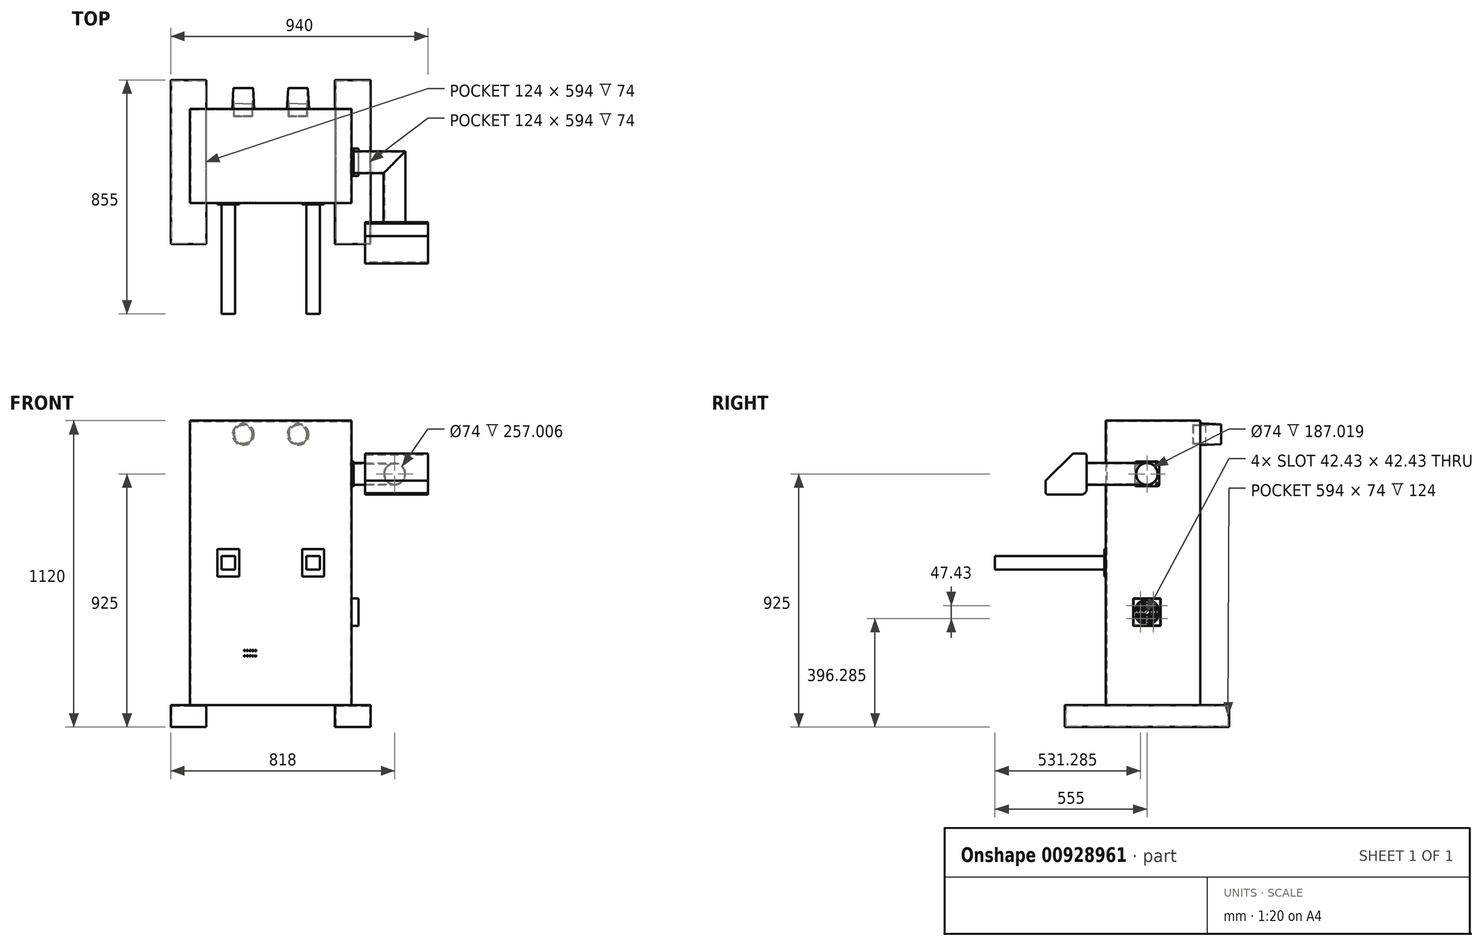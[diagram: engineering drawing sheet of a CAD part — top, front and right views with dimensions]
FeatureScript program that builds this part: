
annotation { "Feature Type Name" : "Feature", "Feature Type Description" : "" }
export const myFeature = defineFeature(function(context is Context, id is Id, definition is map)
    precondition{}
    {
        {
            var Q0;
            Q0=qCreatedBy(makeId("Top.planeOp"),FACE);
            var sketch = newSketch(context, id + "F0", { "sketchPlane" : qUnion([Q0])});
            skLineSegment(sketch, "E0.bottom", {"start": v(-365, 300) * mm, "end": v(-235, 300) * mm});
            skLineSegment(sketch, "E0.top", {"start": v(-365, -300) * mm, "end": v(-235, -300) * mm});
            skLineSegment(sketch, "E0.left", {"start": v(-365, 300) * mm, "end": v(-365, -300) * mm});
            skLineSegment(sketch, "E0.right", {"start": v(-235, 300) * mm, "end": v(-235, -300) * mm});
            skLineSegment(sketch, "E1.bottom", {"start": v(235, 300) * mm, "end": v(365, 300) * mm});
            skLineSegment(sketch, "E1.top", {"start": v(235, -300) * mm, "end": v(365, -300) * mm});
            skLineSegment(sketch, "E1.left", {"start": v(235, 300) * mm, "end": v(235, -300) * mm});
            skLineSegment(sketch, "E1.right", {"start": v(365, 300) * mm, "end": v(365, -300) * mm});
            skLineSegment(sketch, "E2", {"start": v(0, 423) * mm, "end": v(0, -416.4) * mm, "construction": true});
            skLineSegment(sketch, "E3", {"start": v(-423, 0) * mm, "end": v(399.91, 0) * mm, "construction": true});
            skSolve(sketch);
        }
        {
            var Q0;
            Q0 = qSketchRegion(id + "F0", true);
            extrude(context, id + "F1", {"entities" : qUnion([Q0]), "depth" : 80 * mm, "offsetDistance" : 25.4 * mm});
        }
        {
            var Q0;
            Q0=makeQuery(id+"F1.opExtrude","CAP_FACE",FACE,{"disambiguationData":[OSD([sQuery(id+"F0.wireOp",EDGE,"E0.bottom"),sQuery(id+"F0.wireOp",EDGE,"E0.top"),sQuery(id+"F0.wireOp",EDGE,"E0.left"),sQuery(id+"F0.wireOp",EDGE,"E0.right")])],"isStart":false});
            var sketch = newSketch(context, id + "F2", { "sketchPlane" : qUnion([Q0])});
            skLineSegment(sketch, "E4.bottom", {"start": v(-295, 195) * mm, "end": v(295, 195) * mm});
            skLineSegment(sketch, "E4.top", {"start": v(-295, -150) * mm, "end": v(295, -150) * mm});
            skLineSegment(sketch, "E4.left", {"start": v(-295, 195) * mm, "end": v(-295, -150) * mm});
            skLineSegment(sketch, "E4.right", {"start": v(295, 195) * mm, "end": v(295, -150) * mm});
            skSolve(sketch);
        }
        {
            var Q0;
            Q0 = qSketchRegion(id + "F2", true);
            extrude(context, id + "F3", {"entities" : qUnion([Q0]), "operationType" : NewBodyOperationType.ADD, "depth" : 1040 * mm, "offsetDistance" : 25.4 * mm});
        }
        {
            var Q0;
            Q0=makeQuery(id+"F3.opExtrude","SWEPT_FACE",FACE,{"disambiguationData":[OSD([sQuery(id+"F2.wireOp",EDGE,"E4.right")])]});
            var sketch = newSketch(context, id + "F4", { "sketchPlane" : qUnion([Q0])});
            skLineSegment(sketch, "E5.bottom", {"start": v(-38.65, 970) * mm, "end": v(38.65, 970) * mm});
            skLineSegment(sketch, "E5.top", {"start": v(-38.65, 880) * mm, "end": v(38.65, 880) * mm});
            skLineSegment(sketch, "E5.left", {"start": v(-45, 963.65) * mm, "end": v(-45, 886.35) * mm});
            skLineSegment(sketch, "E5.right", {"start": v(45, 963.65) * mm, "end": v(45, 886.35) * mm});
            skLineSegment(sketch, "E6", {"start": v(0, 208.56) * mm, "end": v(0, 602.78) * mm, "construction": true});
            skPoint(sketch, "E7.visualSharp", {"position": v(-45, 970) * mm});
            skArc(sketch, "E7.filletArc", {"start": v(-38.65, 970) * mm, "mid": v(-43.14, 968.14) * mm, "end": v(-45, 963.65) * mm});
            skPoint(sketch, "E8.visualSharp", {"position": v(45, 970) * mm});
            skArc(sketch, "E8.filletArc", {"start": v(45, 963.65) * mm, "mid": v(43.14, 968.14) * mm, "end": v(38.65, 970) * mm});
            skPoint(sketch, "E9.visualSharp", {"position": v(45, 880) * mm});
            skArc(sketch, "E9.filletArc", {"start": v(38.65, 880) * mm, "mid": v(43.14, 881.86) * mm, "end": v(45, 886.35) * mm});
            skPoint(sketch, "E10.visualSharp", {"position": v(-45, 880) * mm});
            skArc(sketch, "E10.filletArc", {"start": v(-45, 886.35) * mm, "mid": v(-43.14, 881.86) * mm, "end": v(-38.65, 880) * mm});
            skSolve(sketch);
        }
        {
            var Q0;
            Q0 = qSketchRegion(id + "F4", true);
            extrude(context, id + "F5", {"entities" : qUnion([Q0]), "operationType" : NewBodyOperationType.ADD, "depth" : 8 * mm, "offsetDistance" : 25.4 * mm});
        }
        {
            var Q0;
            Q0=makeQuery(id+"F5.opExtrude","CAP_FACE",FACE,{"disambiguationData":[OSD([sQuery(id+"F4.wireOp",EDGE,"E5.bottom"),sQuery(id+"F4.wireOp",EDGE,"E5.top"),sQuery(id+"F4.wireOp",EDGE,"E5.left"),sQuery(id+"F4.wireOp",EDGE,"E5.right"),sQuery(id+"F4.wireOp",EDGE,"E7.filletArc"),sQuery(id+"F4.wireOp",EDGE,"E8.filletArc"),sQuery(id+"F4.wireOp",EDGE,"E9.filletArc"),sQuery(id+"F4.wireOp",EDGE,"E10.filletArc")])],"isStart":false});
            var sketch = newSketch(context, id + "F6", { "sketchPlane" : qUnion([Q0])});
            skCircle(sketch, "E11", {"center": v(-38.65, 963.65) * mm, "radius": 5 * mm});
            skCircle(sketch, "E12", {"center": v(38.65, 963.65) * mm, "radius": 5 * mm});
            skCircle(sketch, "E13", {"center": v(38.65, 886.35) * mm, "radius": 5 * mm});
            skCircle(sketch, "E14", {"center": v(-38.65, 886.35) * mm, "radius": 5 * mm});
            skSolve(sketch);
        }
        {
            var Q0;
            Q0 = qSketchRegion(id + "F6", true);
            extrude(context, id + "F7", {"entities" : qUnion([Q0]), "operationType" : NewBodyOperationType.REMOVE, "oppositeDirection" : true, "depth" : 8 * mm, "offsetDistance" : 25.4 * mm});
        }
        {
            var Q0;
            Q0=makeQuery(id+"F5.opExtrude","CAP_FACE",FACE,{"disambiguationData":[OSD([sQuery(id+"F4.wireOp",EDGE,"E5.bottom"),sQuery(id+"F4.wireOp",EDGE,"E5.top"),sQuery(id+"F4.wireOp",EDGE,"E5.left"),sQuery(id+"F4.wireOp",EDGE,"E5.right"),sQuery(id+"F4.wireOp",EDGE,"E7.filletArc"),sQuery(id+"F4.wireOp",EDGE,"E8.filletArc"),sQuery(id+"F4.wireOp",EDGE,"E9.filletArc"),sQuery(id+"F4.wireOp",EDGE,"E10.filletArc")])],"isStart":false});
            var sketch = newSketch(context, id + "F8", { "sketchPlane" : qUnion([Q0])});
            skCircle(sketch, "E15", {"center": v(0, 925) * mm, "radius": 40 * mm});
            skPoint(sketch, "E15.centerSnap0", {"position": v(45, 925) * mm});
            skCircle(sketch, "E16", {"center": v(0, 925) * mm, "radius": 37 * mm});
            skSolve(sketch);
        }
        {
            var Q0;
            Q0=sQuery(id+"F8.wireOp",EDGE,"E16");
            cPlane(context, id + "F9", {"entities" : qUnion([Q0]), "cplaneType" : CPlaneType.LINE_ANGLE, "offset" : 25.4 * mm, "angle" : 0 * degree, "width" : 152.4 * mm, "height" : 152.4 * mm});
        }
        {
            var Q0;
            Q0=qCreatedBy(id+"F9.planeOp",FACE);
            var sketch = newSketch(context, id + "F10", { "sketchPlane" : qUnion([Q0])});
            skLineSegment(sketch, "E17", {"start": v(-303, 925) * mm, "end": v(-453, 925) * mm});
            skSolve(sketch);
        }
        {
            var Q0;
            Q0=makeQuery(id+"F8.imprint","IMPRINT",FACE,{"disambiguationData":[TD([[makeQuery(id+"F8.imprint","IMPRINT",EDGE,{"derivedFrom":sQuery(id+"F8.wireOp",EDGE,"E15")}),-1.0]])]});
            var Q1;
            Q1=sQuery(id+"F10.wireOp",VERTEX,"E17.end");
            cPlane(context, id + "F11", {"entities" : qUnion([Q0, Q1]), "cplaneType" : CPlaneType.PLANE_POINT, "offset" : 25.4 * mm, "width" : 152.4 * mm, "height" : 152.4 * mm});
        }
        {
            var Q0;
            Q0=qCreatedBy(id+"F11.planeOp",FACE);
            var sketch = newSketch(context, id + "F12", { "sketchPlane" : qUnion([Q0])});
            skLineSegment(sketch, "E18", {"start": v(0, 925) * mm, "end": v(-220, 925) * mm});
            skSolve(sketch);
        }
        {
            var Q0;
            Q0=makeQuery(id+"F8.imprint","IMPRINT",FACE,{"disambiguationData":[TD([[makeQuery(id+"F8.imprint","IMPRINT",EDGE,{"derivedFrom":sQuery(id+"F8.wireOp",EDGE,"E15")}),1.0]])]});
            var Q1;
            Q1=sQuery(id+"F10.wireOp",EDGE,"E17");
            var Q2;
            Q2=sQuery(id+"F12.wireOp",EDGE,"E18");
            sweep(context, id + "F13", {"operationType" : NewBodyOperationType.ADD, "profiles" : qUnion([Q0]), "path" : qUnion([Q1, Q2])});
        }
        {
            var Q0;
            Q0=makeQuery(id+"F3.opExtrude","SWEPT_FACE",FACE,{"disambiguationData":[OSD([sQuery(id+"F2.wireOp",EDGE,"E4.right")])]});
            var sketch = newSketch(context, id + "F14", { "sketchPlane" : qUnion([Q0])});
            skLineSegment(sketch, "E19.bottom", {"start": v(-50, 470) * mm, "end": v(50, 470) * mm});
            skLineSegment(sketch, "E19.top", {"start": v(-50, 370) * mm, "end": v(50, 370) * mm});
            skLineSegment(sketch, "E19.left", {"start": v(-50, 470) * mm, "end": v(-50, 370) * mm});
            skLineSegment(sketch, "E19.right", {"start": v(50, 470) * mm, "end": v(50, 370) * mm});
            skLineSegment(sketch, "E20", {"start": v(0, 221.64) * mm, "end": v(0, 996.3) * mm, "construction": true});
            skLineSegment(sketch, "E21.bottom", {"start": v(49, 371) * mm, "end": v(-49, 371) * mm});
            skLineSegment(sketch, "E21.top", {"start": v(49, 469) * mm, "end": v(-49, 469) * mm});
            skLineSegment(sketch, "E21.left", {"start": v(49, 371) * mm, "end": v(49, 469) * mm});
            skLineSegment(sketch, "E21.right", {"start": v(-49, 371) * mm, "end": v(-49, 469) * mm});
            skPoint(sketch, "E21.middle", {"position": v(0, 420) * mm});
            skPoint(sketch, "E21.middle.positionSnap0", {"position": v(50, 420) * mm});
            skPoint(sketch, "E21.centerSnap0", {"position": v(50, 420) * mm});
            skSolve(sketch);
        }
        {
            var Q0;
            Q0 = qSketchRegion(id + "F14", true);
            extrude(context, id + "F15", {"entities" : qUnion([Q0]), "operationType" : NewBodyOperationType.ADD, "depth" : 25.4 * mm, "offsetDistance" : 25.4 * mm});
        }
        {
            var Q0;
            Q0=makeQuery(id+"F15.opExtrude","CAP_FACE",FACE,{"disambiguationData":[OSD([sQuery(id+"F14.wireOp",EDGE,"E19.bottom"),sQuery(id+"F14.wireOp",EDGE,"E19.top"),sQuery(id+"F14.wireOp",EDGE,"E19.left"),sQuery(id+"F14.wireOp",EDGE,"E19.right"),sQuery(id+"F14.wireOp",EDGE,"E21.bottom"),sQuery(id+"F14.wireOp",EDGE,"E21.top"),sQuery(id+"F14.wireOp",EDGE,"E21.left"),sQuery(id+"F14.wireOp",EDGE,"E21.right")])],"isStart":false});
            var sketch = newSketch(context, id + "F16", { "sketchPlane" : qUnion([Q0])});
            skLineSegment(sketch, "E22.bottom", {"start": v(-49, 469) * mm, "end": v(49, 469) * mm});
            skLineSegment(sketch, "E22.top", {"start": v(-49, 371) * mm, "end": v(49, 371) * mm});
            skLineSegment(sketch, "E22.left", {"start": v(-49, 469) * mm, "end": v(-49, 371) * mm});
            skLineSegment(sketch, "E22.right", {"start": v(49, 469) * mm, "end": v(49, 371) * mm});
            skSolve(sketch);
        }
        {
            var Q0;
            Q0 = qSketchRegion(id + "F16", true);
            extrude(context, id + "F17", {"entities" : qUnion([Q0]), "depth" : 1 * mm, "offsetDistance" : 25.4 * mm});
        }
        {
            var Q0;
            Q0=makeQuery(id+"F17.opExtrude","CAP_FACE",FACE,{"disambiguationData":[OSD([sQuery(id+"F16.wireOp",EDGE,"E22.bottom"),sQuery(id+"F16.wireOp",EDGE,"E22.top"),sQuery(id+"F16.wireOp",EDGE,"E22.left"),sQuery(id+"F16.wireOp",EDGE,"E22.right")])],"isStart":false});
            var sketch = newSketch(context, id + "F18", { "sketchPlane" : qUnion([Q0])});
            skCircle(sketch, "E23", {"center": v(0, 420) * mm, "radius": 10 * mm});
            skPoint(sketch, "E23.centerSnap0", {"position": v(49, 420) * mm});
            skArc(sketch, "E24", {"start": v(-2.5, 434.8) * mm, "mid": v(-10.6, 430.6) * mm, "end": v(-14.8, 422.5) * mm});
            skArc(sketch, "E25.0", {"start": v(-2.5, 439.84) * mm, "mid": v(-14.14, 434.14) * mm, "end": v(-19.84, 422.5) * mm});
            skArc(sketch, "E26.0", {"start": v(-2.5, 444.87) * mm, "mid": v(-17.68, 437.68) * mm, "end": v(-24.87, 422.5) * mm});
            skArc(sketch, "E27.0", {"start": v(-2.5, 449.9) * mm, "mid": v(-21.21, 441.21) * mm, "end": v(-29.9, 422.5) * mm});
            skArc(sketch, "E28.0", {"start": v(-2.5, 454.91) * mm, "mid": v(-24.75, 444.75) * mm, "end": v(-34.91, 422.5) * mm});
            skArc(sketch, "E29.0", {"start": v(-2.5, 459.92) * mm, "mid": v(-28.28, 448.28) * mm, "end": v(-39.92, 422.5) * mm});
            skArc(sketch, "E30.0", {"start": v(-2.5, 464.93) * mm, "mid": v(-31.82, 451.82) * mm, "end": v(-44.93, 422.5) * mm});
            skCircle(sketch, "E31.0", {"center": v(0, 420) * mm, "radius": 49 * mm});
            skLineSegment(sketch, "E32", {"start": v(0, 469) * mm, "end": v(0, 375) * mm, "construction": true});
            skLineSegment(sketch, "E33.bottom", {"start": v(-2.5, 469) * mm, "end": v(2.5, 469) * mm});
            skLineSegment(sketch, "E33.left", {"start": v(-2.5, 469) * mm, "end": v(-2.5, 429.68) * mm});
            skLineSegment(sketch, "E33.right", {"start": v(2.5, 469) * mm, "end": v(2.5, 429.68) * mm});
            skPoint(sketch, "E34.orphan", {"position": v(2.5, 420) * mm});
            skLineSegment(sketch, "E35", {"start": v(53.82, 420) * mm, "end": v(-49, 420) * mm, "construction": true});
            skLineSegment(sketch, "E36.bottom", {"start": v(9.68, 422.5) * mm, "end": v(49, 422.5) * mm});
            skLineSegment(sketch, "E36.top", {"start": v(9.68, 417.5) * mm, "end": v(49, 417.5) * mm});
            skLineSegment(sketch, "E36.right", {"start": v(49, 422.5) * mm, "end": v(49, 417.5) * mm});
            skArc(sketch, "E37.trimOffspring", {"start": v(44.93, 422.5) * mm, "mid": v(31.82, 451.82) * mm, "end": v(2.5, 464.93) * mm});
            skArc(sketch, "E38.trimOffspring", {"start": v(39.92, 422.5) * mm, "mid": v(28.28, 448.28) * mm, "end": v(2.5, 459.92) * mm});
            skArc(sketch, "E39.trimOffspring", {"start": v(34.91, 422.5) * mm, "mid": v(24.75, 444.75) * mm, "end": v(2.5, 454.91) * mm});
            skArc(sketch, "E40.trimOffspring", {"start": v(29.9, 422.5) * mm, "mid": v(21.21, 441.21) * mm, "end": v(2.5, 449.9) * mm});
            skArc(sketch, "E41.trimOffspring", {"start": v(24.87, 422.5) * mm, "mid": v(17.68, 437.68) * mm, "end": v(2.5, 444.87) * mm});
            skArc(sketch, "E42.trimOffspring", {"start": v(19.84, 422.5) * mm, "mid": v(14.14, 434.14) * mm, "end": v(2.5, 439.84) * mm});
            skArc(sketch, "E43.trimOffspring", {"start": v(14.8, 422.5) * mm, "mid": v(10.6, 430.6) * mm, "end": v(2.5, 434.8) * mm});
            skPoint(sketch, "E44", {"position": v(0, 371) * mm});
            skLineSegment(sketch, "E45.top", {"start": v(-2.5, 371) * mm, "end": v(2.5, 371) * mm});
            skLineSegment(sketch, "E45.left", {"start": v(-2.5, 410.32) * mm, "end": v(-2.5, 371) * mm});
            skLineSegment(sketch, "E45.right", {"start": v(2.5, 410.32) * mm, "end": v(2.5, 371) * mm});
            skArc(sketch, "E46.trimOffspring", {"start": v(2.5, 375.07) * mm, "mid": v(31.82, 388.18) * mm, "end": v(44.93, 417.5) * mm});
            skArc(sketch, "E47.trimOffspring", {"start": v(2.5, 380.08) * mm, "mid": v(28.28, 391.72) * mm, "end": v(39.92, 417.5) * mm});
            skArc(sketch, "E48.trimOffspring", {"start": v(2.5, 385.09) * mm, "mid": v(24.75, 395.25) * mm, "end": v(34.91, 417.5) * mm});
            skArc(sketch, "E49.trimOffspring", {"start": v(2.5, 390.1) * mm, "mid": v(21.21, 398.79) * mm, "end": v(29.9, 417.5) * mm});
            skArc(sketch, "E50.trimOffspring", {"start": v(2.5, 395.13) * mm, "mid": v(17.68, 402.32) * mm, "end": v(24.87, 417.5) * mm});
            skArc(sketch, "E51.trimOffspring", {"start": v(2.5, 400.16) * mm, "mid": v(14.14, 405.86) * mm, "end": v(19.84, 417.5) * mm});
            skArc(sketch, "E52.trimOffspring", {"start": v(2.5, 405.2) * mm, "mid": v(10.6, 409.4) * mm, "end": v(14.8, 417.5) * mm});
            skLineSegment(sketch, "E53.bottom", {"start": v(-9.68, 422.5) * mm, "end": v(-49, 422.5) * mm});
            skLineSegment(sketch, "E53.top", {"start": v(-9.68, 417.5) * mm, "end": v(-49, 417.5) * mm});
            skLineSegment(sketch, "E53.right", {"start": v(-49, 422.5) * mm, "end": v(-49, 417.5) * mm});
            skArc(sketch, "E54.trimOffspring", {"start": v(-44.93, 417.5) * mm, "mid": v(-31.82, 388.18) * mm, "end": v(-2.5, 375.07) * mm});
            skArc(sketch, "E55.trimOffspring", {"start": v(-39.92, 417.5) * mm, "mid": v(-28.28, 391.72) * mm, "end": v(-2.5, 380.08) * mm});
            skArc(sketch, "E56.trimOffspring", {"start": v(-34.91, 417.5) * mm, "mid": v(-24.75, 395.25) * mm, "end": v(-2.5, 385.09) * mm});
            skArc(sketch, "E57.trimOffspring", {"start": v(-29.9, 417.5) * mm, "mid": v(-21.21, 398.79) * mm, "end": v(-2.5, 390.1) * mm});
            skArc(sketch, "E58.trimOffspring", {"start": v(-24.87, 417.5) * mm, "mid": v(-17.68, 402.32) * mm, "end": v(-2.5, 395.13) * mm});
            skArc(sketch, "E59.trimOffspring", {"start": v(-19.84, 417.5) * mm, "mid": v(-14.14, 405.86) * mm, "end": v(-2.5, 400.16) * mm});
            skArc(sketch, "E60.trimOffspring", {"start": v(-14.8, 417.5) * mm, "mid": v(-10.6, 409.4) * mm, "end": v(-2.5, 405.2) * mm});
            skSolve(sketch);
        }
        {
            var Q0;
            {var subQ0=sQuery(id+"F18.wireOp",EDGE,"E37.trimOffspring");Q0=makeQuery(id+"F18.imprint","IMPRINT",FACE,{"disambiguationData":[TD([[makeQuery(id+"F18.imprint","IMPRINT",EDGE,{"derivedFrom":subQ0}),1.0]])]});}
            var Q1;
            {var subQ0=sQuery(id+"F18.wireOp",EDGE,"E39.trimOffspring");Q1=makeQuery(id+"F18.imprint","IMPRINT",FACE,{"disambiguationData":[TD([[makeQuery(id+"F18.imprint","IMPRINT",EDGE,{"derivedFrom":subQ0}),1.0]])]});}
            var Q2;
            {var subQ0=sQuery(id+"F18.wireOp",EDGE,"E41.trimOffspring");Q2=makeQuery(id+"F18.imprint","IMPRINT",FACE,{"disambiguationData":[TD([[makeQuery(id+"F18.imprint","IMPRINT",EDGE,{"derivedFrom":subQ0}),1.0]])]});}
            var Q3;
            {var subQ5=sQuery(id+"F18.wireOp",EDGE,"E43.trimOffspring");Q3=makeQuery(id+"F18.imprint","IMPRINT",FACE,{"disambiguationData":[TD([[makeQuery(id+"F18.imprint","IMPRINT",EDGE,{"derivedFrom":subQ5}),1.0]])]});}
            var Q4;
            {var subQ0=sQuery(id+"F18.wireOp",EDGE,"E46.trimOffspring");Q4=makeQuery(id+"F18.imprint","IMPRINT",FACE,{"disambiguationData":[TD([[makeQuery(id+"F18.imprint","IMPRINT",EDGE,{"derivedFrom":subQ0}),1.0]])]});}
            var Q5;
            {var subQ0=sQuery(id+"F18.wireOp",EDGE,"E48.trimOffspring");Q5=makeQuery(id+"F18.imprint","IMPRINT",FACE,{"disambiguationData":[TD([[makeQuery(id+"F18.imprint","IMPRINT",EDGE,{"derivedFrom":subQ0}),1.0]])]});}
            var Q6;
            {var subQ0=sQuery(id+"F18.wireOp",EDGE,"E50.trimOffspring");Q6=makeQuery(id+"F18.imprint","IMPRINT",FACE,{"disambiguationData":[TD([[makeQuery(id+"F18.imprint","IMPRINT",EDGE,{"derivedFrom":subQ0}),1.0]])]});}
            var Q7;
            {var subQ5=sQuery(id+"F18.wireOp",EDGE,"E52.trimOffspring");Q7=makeQuery(id+"F18.imprint","IMPRINT",FACE,{"disambiguationData":[TD([[makeQuery(id+"F18.imprint","IMPRINT",EDGE,{"derivedFrom":subQ5}),1.0]])]});}
            var Q8;
            {var subQ0=sQuery(id+"F18.wireOp",EDGE,"E54.trimOffspring");Q8=makeQuery(id+"F18.imprint","IMPRINT",FACE,{"disambiguationData":[TD([[makeQuery(id+"F18.imprint","IMPRINT",EDGE,{"derivedFrom":subQ0}),1.0]])]});}
            var Q9;
            {var subQ0=sQuery(id+"F18.wireOp",EDGE,"E56.trimOffspring");Q9=makeQuery(id+"F18.imprint","IMPRINT",FACE,{"disambiguationData":[TD([[makeQuery(id+"F18.imprint","IMPRINT",EDGE,{"derivedFrom":subQ0}),1.0]])]});}
            var Q10;
            {var subQ0=sQuery(id+"F18.wireOp",EDGE,"E58.trimOffspring");Q10=makeQuery(id+"F18.imprint","IMPRINT",FACE,{"disambiguationData":[TD([[makeQuery(id+"F18.imprint","IMPRINT",EDGE,{"derivedFrom":subQ0}),1.0]])]});}
            var Q11;
            {var subQ5=sQuery(id+"F18.wireOp",EDGE,"E60.trimOffspring");Q11=makeQuery(id+"F18.imprint","IMPRINT",FACE,{"disambiguationData":[TD([[makeQuery(id+"F18.imprint","IMPRINT",EDGE,{"derivedFrom":subQ5}),1.0]])]});}
            var Q12;
            {var subQ0=sQuery(id+"F18.wireOp",EDGE,"E29.0");Q12=makeQuery(id+"F18.imprint","IMPRINT",FACE,{"disambiguationData":[TD([[makeQuery(id+"F18.imprint","IMPRINT",EDGE,{"derivedFrom":subQ0}),-1.0]])]});}
            var Q13;
            {var subQ0=sQuery(id+"F18.wireOp",EDGE,"E27.0");Q13=makeQuery(id+"F18.imprint","IMPRINT",FACE,{"disambiguationData":[TD([[makeQuery(id+"F18.imprint","IMPRINT",EDGE,{"derivedFrom":subQ0}),-1.0]])]});}
            var Q14;
            {var subQ0=sQuery(id+"F18.wireOp",EDGE,"E25.0");Q14=makeQuery(id+"F18.imprint","IMPRINT",FACE,{"disambiguationData":[TD([[makeQuery(id+"F18.imprint","IMPRINT",EDGE,{"derivedFrom":subQ0}),-1.0]])]});}
            var Q15;
            {var subQ5=sQuery(id+"F18.wireOp",EDGE,"E24");Q15=makeQuery(id+"F18.imprint","IMPRINT",FACE,{"disambiguationData":[TD([[makeQuery(id+"F18.imprint","IMPRINT",EDGE,{"derivedFrom":subQ5}),1.0]])]});}
            extrude(context, id + "F19", {"entities" : qUnion([Q0, Q1, Q2, Q3, Q4, Q5, Q6, Q7, Q8, Q9, Q10, Q11, Q12, Q13, Q14, Q15]), "operationType" : NewBodyOperationType.REMOVE, "oppositeDirection" : true, "depth" : 25.4 * mm, "offsetDistance" : 25.4 * mm});
        }
        {
            var Q0;
            Q0=makeQuery(id+"F3.opExtrude","SWEPT_FACE",FACE,{"disambiguationData":[OSD([sQuery(id+"F2.wireOp",EDGE,"E4.bottom")])]});
            var sketch = newSketch(context, id + "F20", { "sketchPlane" : qUnion([Q0])});
            skLineSegment(sketch, "E61", {"start": v(0, 1376.82) * mm, "end": v(0, -627.26) * mm, "construction": true});
            skPoint(sketch, "E61.startSnap0", {"position": v(0, 1120) * mm});
            skCircle(sketch, "E62", {"center": v(-100, 1070) * mm, "radius": 40 * mm});
            skCircle(sketch, "E63", {"center": v(100, 1070) * mm, "radius": 40 * mm});
            skCircle(sketch, "E64", {"center": v(-100, 1070) * mm, "radius": 32 * mm});
            skCircle(sketch, "E65", {"center": v(100, 1070) * mm, "radius": 32 * mm});
            skSolve(sketch);
        }
        {
            var Q0;
            Q0=makeQuery(id+"F20.imprint","IMPRINT",FACE,{"disambiguationData":[TD([[makeQuery(id+"F20.imprint","IMPRINT",EDGE,{"derivedFrom":sQuery(id+"F20.wireOp",EDGE,"E64")}),1.0]])]});
            var Q1;
            Q1=makeQuery(id+"F20.imprint","IMPRINT",FACE,{"disambiguationData":[TD([[makeQuery(id+"F20.imprint","IMPRINT",EDGE,{"derivedFrom":sQuery(id+"F20.wireOp",EDGE,"E65")}),1.0]])]});
            extrude(context, id + "F21", {"entities" : qUnion([Q0, Q1]), "operationType" : NewBodyOperationType.REMOVE, "oppositeDirection" : true, "depth" : 25.4 * mm, "offsetDistance" : 25.4 * mm});
        }
        {
            var Q0;
            Q0 = qSketchRegion(id + "F20", true);
            extrude(context, id + "F22", {"entities" : qUnion([Q0]), "operationType" : NewBodyOperationType.ADD, "depth" : 100 * mm, "offsetDistance" : 25.4 * mm, "hasDraft" : true, "draftAngle" : 3 * degree, "draftPullDirection" : true});
        }
        {
            var Q0;
            Q0=makeQuery(id+"F3.opExtrude","CAP_FACE",FACE,{"disambiguationData":[OSD([sQuery(id+"F2.wireOp",EDGE,"E4.bottom"),sQuery(id+"F2.wireOp",EDGE,"E4.top"),sQuery(id+"F2.wireOp",EDGE,"E4.left"),sQuery(id+"F2.wireOp",EDGE,"E4.right")])],"isStart":true});
            shell(context, id + "F23", {"entities" : qUnion([Q0]), "thickness" : 3 * mm});
        }
        {
            var Q0;
            Q0=makeQuery(id+"F3.opExtrude","SWEPT_FACE",FACE,{"disambiguationData":[OSD([sQuery(id+"F2.wireOp",EDGE,"E4.top")])]});
            var sketch = newSketch(context, id + "F24", { "sketchPlane" : qUnion([Q0])});
            skCircle(sketch, "E66", {"center": v(-95, 280) * mm, "radius": 2.5 * mm});
            skCircle(sketch, "E67", {"center": v(-85, 280) * mm, "radius": 2.5 * mm});
            skCircle(sketch, "E68", {"center": v(-75, 280) * mm, "radius": 2.5 * mm});
            skCircle(sketch, "E69", {"center": v(-65, 280) * mm, "radius": 2.5 * mm});
            skCircle(sketch, "E70", {"center": v(-55, 280) * mm, "radius": 2.47 * mm});
            skCircle(sketch, "E71", {"center": v(-95, 260) * mm, "radius": 2.5 * mm});
            skCircle(sketch, "E72", {"center": v(-85, 260) * mm, "radius": 2.5 * mm});
            skCircle(sketch, "E73", {"center": v(-75, 260) * mm, "radius": 2.5 * mm});
            skCircle(sketch, "E74", {"center": v(-65, 260) * mm, "radius": 2.5 * mm});
            skCircle(sketch, "E75", {"center": v(-55, 260) * mm, "radius": 2.5 * mm});
            skSolve(sketch);
        }
        {
            var Q0;
            Q0 = qSketchRegion(id + "F24", true);
            extrude(context, id + "F25", {"entities" : qUnion([Q0]), "operationType" : NewBodyOperationType.REMOVE, "oppositeDirection" : true, "depth" : 25.4 * mm, "offsetDistance" : 25.4 * mm});
        }
        {
            var Q0;
            Q0=makeQuery(id+"F13.opSweep","CAP_FACE",FACE,{"disambiguationData":[OSD([sQuery(id+"F8.wireOp",EDGE,"E15"),sQuery(id+"F8.wireOp",EDGE,"E16"),sQuery(id+"F12.wireOp",VERTEX,"E18.end")])],"isStart":false});
            cPlane(context, id + "F26", {"entities" : qUnion([Q0]), "cplaneType" : CPlaneType.OFFSET, "offset" : 0 * mm, "width" : 152.4 * mm, "height" : 152.4 * mm});
        }
        {
            var Q0;
            Q0=qCreatedBy(id+"F26.planeOp",FACE);
            var sketch = newSketch(context, id + "F27", { "sketchPlane" : qUnion([Q0])});
            skLineSegment(sketch, "E76.bottom", {"start": v(345, 1000) * mm, "end": v(575, 1000) * mm});
            skLineSegment(sketch, "E76.top", {"start": v(345, 850) * mm, "end": v(575, 850) * mm});
            skLineSegment(sketch, "E76.left", {"start": v(345, 1000) * mm, "end": v(345, 850) * mm});
            skLineSegment(sketch, "E76.right", {"start": v(575, 1000) * mm, "end": v(575, 850) * mm});
            skSolve(sketch);
        }
        {
            var Q0;
            Q0 = qSketchRegion(id + "F27", true);
            extrude(context, id + "F28", {"entities" : qUnion([Q0]), "operationType" : NewBodyOperationType.ADD, "depth" : 150 * mm, "offsetDistance" : 25.4 * mm});
        }
        {
            var Q0;
            Q0=makeQuery(id+"F28.opExtrude","SWEPT_FACE",FACE,{"disambiguationData":[OSD([sQuery(id+"F27.wireOp",EDGE,"E76.right")])]});
            var sketch = newSketch(context, id + "F29", { "sketchPlane" : qUnion([Q0])});
            skLineSegment(sketch, "E77", {"start": v(-370, 850) * mm, "end": v(-270, 850) * mm});
            skLineSegment(sketch, "E78", {"start": v(-220, 900) * mm, "end": v(-220, 1000) * mm});
            skLineSegment(sketch, "E79", {"start": v(-370, 1000) * mm, "end": v(-220, 1000) * mm});
            skLineSegment(sketch, "E80", {"start": v(-370, 1000) * mm, "end": v(-370, 850) * mm});
            skPoint(sketch, "E81.visualSharp", {"position": v(-220, 850) * mm});
            skArc(sketch, "E81.filletArc", {"start": v(-270, 850) * mm, "mid": v(-234.64, 864.64) * mm, "end": v(-220, 900) * mm});
            skLineSegment(sketch, "E82", {"start": v(-370, 900) * mm, "end": v(-270, 1000) * mm});
            skSolve(sketch);
        }
        {
            var Q0;
            {var subQ3=sQuery(id+"F29.wireOp",EDGE,"E82");Q0=makeQuery(id+"F29.imprint","IMPRINT",FACE,{"disambiguationData":[TD([[makeQuery(id+"F29.imprint","IMPRINT",EDGE,{"derivedFrom":subQ3}),1.0]])]});}
            extrude(context, id + "F30", {"entities" : qUnion([Q0]), "operationType" : NewBodyOperationType.REMOVE, "endBound" : BoundingType.UP_TO_NEXT, "oppositeDirection" : true, "depth" : 25.4 * mm, "offsetDistance" : 25.4 * mm});
        }
        {
            var Q0;
            Q0=makeQuery(id+"F28.opExtrude","CAP_EDGE",EDGE,{"disambiguationData":[OSD([sQuery(id+"F27.wireOp",EDGE,"E76.top")])],"isStart":true});
            fillet(context, id + "F31", {"entities" : qUnion([Q0]), "radius" : 20 * mm, "tangentPropagation" : true, "allowEdgeOverflow" : false});
        }
        {
            var Q0;
            {var subQ0=sQuery(id+"F27.wireOp",EDGE,"E76.top");Q0=makeQuery(id+"F30.boolean.opBoolean","MERGE",EDGE,{"derivedFrom":[makeQuery(id+"F28.opExtrude","CAP_EDGE",EDGE,{"disambiguationData":[OSD([subQ0])],"isStart":false})],"fromTools":[makeQuery(id+"F30.opExtrude","SWEPT_EDGE",EDGE,{"disambiguationData":[OSD([subQ0,sQuery(id+"F27.wireOp",EDGE,"E76.right"),sQuery(id+"F29.wireOp",EDGE,"E77"),sQuery(id+"F29.wireOp",EDGE,"yaYKsTQe-KL1j-xqfh-EybX-QsPIRCIB8Hmb"),sQuery(id+"F29.wireOp",EDGE,"E80")])]})]});}
            var Q1;
            {var subQ0=sQuery(id+"F27.wireOp",EDGE,"E76.bottom");Q1=makeQuery(id+"F30.boolean.opBoolean","MERGE",EDGE,{"derivedFrom":[makeQuery(id+"F28.opExtrude","CAP_EDGE",EDGE,{"disambiguationData":[OSD([subQ0])],"isStart":true})],"fromTools":[makeQuery(id+"F30.opExtrude","SWEPT_EDGE",EDGE,{"disambiguationData":[OSD([subQ0,sQuery(id+"F27.wireOp",EDGE,"E76.left")])]})]});}
            chamfer(context, id + "F32", {"entities" : qUnion([Q0, Q1]), "width" : 5.08 * mm, "tangentPropagation" : true});
        }
        {
            var Q0;
            Q0=makeQuery(id+"F3.opExtrude","SWEPT_FACE",FACE,{"disambiguationData":[OSD([sQuery(id+"F2.wireOp",EDGE,"E4.top")])]});
            var sketch = newSketch(context, id + "F33", { "sketchPlane" : qUnion([Q0])});
            skLineSegment(sketch, "E83.bottom", {"start": v(115, 550) * mm, "end": v(195, 550) * mm});
            skLineSegment(sketch, "E83.top", {"start": v(115, 650) * mm, "end": v(195, 650) * mm});
            skLineSegment(sketch, "E83.left", {"start": v(115, 650) * mm, "end": v(115, 550) * mm});
            skLineSegment(sketch, "E83.right", {"start": v(195, 650) * mm, "end": v(195, 550) * mm});
            skLineSegment(sketch, "E84", {"start": v(0, 1311.23) * mm, "end": v(0, -170.46) * mm, "construction": true});
            skLineSegment(sketch, "E85.bottom", {"start": v(-115, 650) * mm, "end": v(-195, 650) * mm});
            skLineSegment(sketch, "E85.top", {"start": v(-115, 550) * mm, "end": v(-195, 550) * mm});
            skLineSegment(sketch, "E85.left", {"start": v(-115, 650) * mm, "end": v(-115, 550) * mm});
            skLineSegment(sketch, "E85.right", {"start": v(-195, 650) * mm, "end": v(-195, 550) * mm});
            skSolve(sketch);
        }
        {
            var Q0;
            Q0 = qSketchRegion(id + "F33", true);
            extrude(context, id + "F34", {"entities" : qUnion([Q0]), "operationType" : NewBodyOperationType.ADD, "depth" : 5 * mm, "offsetDistance" : 25.4 * mm});
        }
        {
            var Q0;
            Q0=makeQuery(id+"F34.opExtrude","CAP_FACE",FACE,{"disambiguationData":[OSD([sQuery(id+"F33.wireOp",EDGE,"E85.bottom"),sQuery(id+"F33.wireOp",EDGE,"E85.top"),sQuery(id+"F33.wireOp",EDGE,"E85.left"),sQuery(id+"F33.wireOp",EDGE,"E85.right")])],"isStart":false});
            var sketch = newSketch(context, id + "F35", { "sketchPlane" : qUnion([Q0])});
            skLineSegment(sketch, "E86.bottom", {"start": v(-180, 625) * mm, "end": v(-130, 625) * mm});
            skLineSegment(sketch, "E86.top", {"start": v(-180, 575) * mm, "end": v(-130, 575) * mm});
            skLineSegment(sketch, "E86.left", {"start": v(-180, 625) * mm, "end": v(-180, 575) * mm});
            skLineSegment(sketch, "E86.right", {"start": v(-130, 625) * mm, "end": v(-130, 575) * mm});
            skLineSegment(sketch, "E87.bottom", {"start": v(130, 625) * mm, "end": v(180, 625) * mm});
            skLineSegment(sketch, "E87.top", {"start": v(130, 575) * mm, "end": v(180, 575) * mm});
            skLineSegment(sketch, "E87.left", {"start": v(130, 625) * mm, "end": v(130, 575) * mm});
            skLineSegment(sketch, "E87.right", {"start": v(180, 625) * mm, "end": v(180, 575) * mm});
            skLineSegment(sketch, "E88", {"start": v(-155, 690.53) * mm, "end": v(-155, 487.93) * mm, "construction": true});
            skPoint(sketch, "E88.startSnap0", {"position": v(-155, 650) * mm});
            skLineSegment(sketch, "E89", {"start": v(-224.09, 600) * mm, "end": v(-61, 600) * mm, "construction": true});
            skPoint(sketch, "E89.startSnap0", {"position": v(-195, 600) * mm});
            skLineSegment(sketch, "E90", {"start": v(155, 732.5) * mm, "end": v(155, 402.97) * mm, "construction": true});
            skLineSegment(sketch, "E91", {"start": v(92.5, 600) * mm, "end": v(226.95, 600) * mm, "construction": true});
            skSolve(sketch);
        }
        {
            var Q0;
            Q0 = qSketchRegion(id + "F35", true);
            extrude(context, id + "F36", {"entities" : qUnion([Q0]), "operationType" : NewBodyOperationType.ADD, "depth" : 400 * mm, "offsetDistance" : 25.4 * mm});
        }
    });
